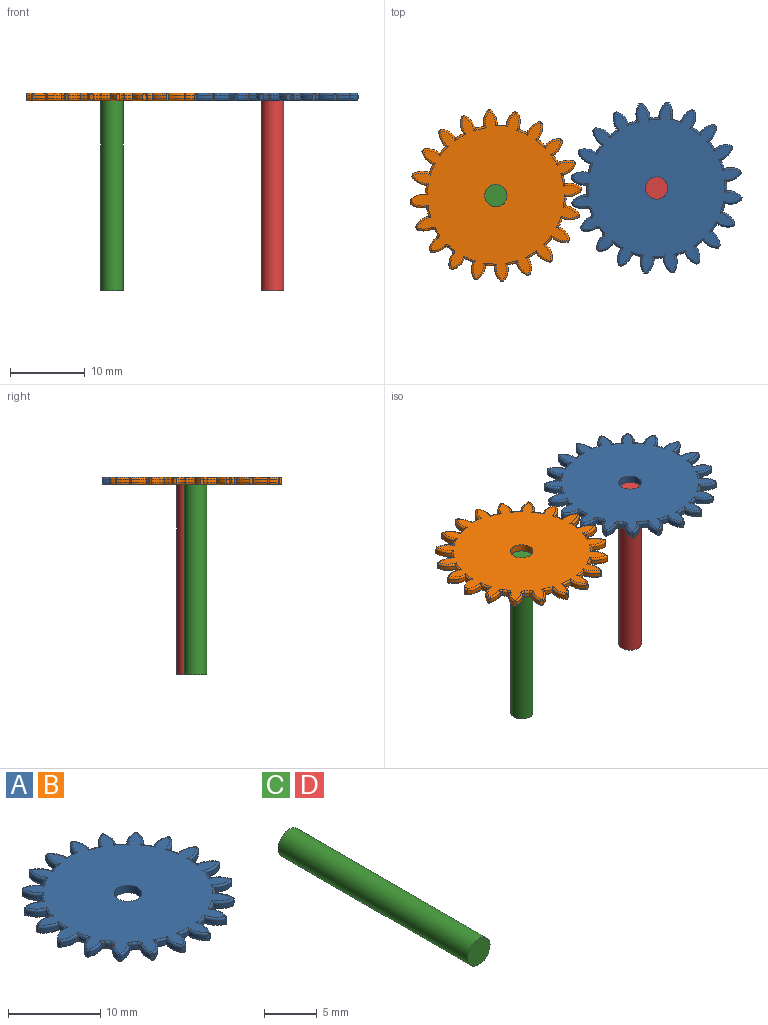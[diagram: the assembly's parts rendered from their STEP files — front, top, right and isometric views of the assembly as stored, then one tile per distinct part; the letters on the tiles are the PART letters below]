
ASSEMBLY  parts=4 mates=2
PART A: 214 faces, bbox 23.5x23.5x1 mm
  f0: cylinder r=2.61mm len=2.18mm, axis (0,0,-1), area 1.2mm2, adj f1,f79,f96,f200
  f1: cylinder r=9.41mm len=1.14mm, axis (0,0,-1), area 0.6mm2, adj f0,f2,f95,f201
  f2: cylinder r=2.61mm len=1.71mm, axis (0,0,-1), area 1.2mm2, adj f1,f3,f94,f203
  f3: plane 0.97x0.41mm, normal (-0.38,0.92,0), area 0.4mm2, adj f2,f4,f93,f94,f203,f205
  f4: cylinder r=2.61mm len=2.23mm, axis (0,0,-1), area 1.2mm2, adj f3,f5,f93,f205
  f5: cylinder r=9.41mm len=1mm, axis (0,0,-1), area 0.6mm2, adj f4,f6,f92,f207
  f6: cylinder r=2.61mm len=1.89mm, axis (0,0,-1), area 1.2mm2, adj f5,f7,f91,f209
  f7: plane 0.97x0.34mm, normal (-0.65,0.76,0), area 0.4mm2, adj f6,f8,f90,f91,f209,f211
  f8: cylinder r=2.61mm len=2.06mm, axis (0,0,-1), area 1.2mm2, adj f7,f9,f90,f211
  f9: cylinder r=9.41mm len=0.89mm, axis (0,0,-1), area 0.6mm2, adj f8,f10,f89,f213
  f10: cylinder r=2.61mm len=2.17mm, axis (0,0,-1), area 1.2mm2, adj f9,f11,f88,f212
  f11: plane 0.97x0.38mm, normal (-0.85,0.52,0), area 0.4mm2, adj f10,f12,f87,f88,f210,f212
  f12: cylinder r=2.61mm len=1.68mm, axis (0,0,-1), area 1.2mm2, adj f11,f13,f87,f210
  f13: cylinder r=9.41mm len=1.08mm, axis (0,0,-1), area 0.6mm2, adj f12,f14,f86,f208
  f14: cylinder r=2.61mm len=2.23mm, axis (0,0,-1), area 1.2mm2, adj f13,f15,f85,f206
  f15: plane 0.97x0.43mm, normal (-0.97,0.23,0), area 0.4mm2, adj f14,f16,f84,f85,f204,f206
  f16: cylinder r=2.61mm len=1.92mm, axis (0,0,-1), area 1.2mm2, adj f15,f17,f84,f204
  f17: cylinder r=9.41mm len=1.17mm, axis (0,0,-1), area 0.6mm2, adj f16,f18,f83,f202
  f18: cylinder r=2.61mm len=2.32mm, axis (0,0,-1), area 2.3mm2, adj f17,f19,f81,f82,f83,f169,f202
  f19: plane 0.75x0.44mm, normal (-1,-0.08,0), area 0.3mm2, adj f18,f20,f82,f169,f192
  f20: cylinder r=2.61mm len=2.18mm, axis (0,0,-1), area 1.2mm2, adj f19,f21,f173,f192
  f21: cylinder r=9.41mm len=1.14mm, axis (0,0,-1), area 0.6mm2, adj f20,f22,f176,f195
  f22: cylinder r=2.61mm len=1.71mm, axis (0,0,-1), area 1.2mm2, adj f21,f23,f180,f197
  f23: plane 0.73x0.41mm, normal (-0.92,-0.38,0), area 0.3mm2, adj f22,f24,f183,f197,f198
  f24: cylinder r=2.61mm len=2.02mm, axis (0,0,-1), area 1mm2, adj f23,f186,f193,f198
  f25: cylinder r=9.41mm len=0.59mm, axis (0,0,-1), area 0.3mm2, adj f187,f188,f193,f194
  f26: cylinder r=2.61mm len=1.76mm, axis (0,0,-1), area 1mm2, adj f27,f181,f188,f189
  f27: plane 0.97x0.34mm, normal (-0.76,-0.65,0), area 0.4mm2, adj f26,f28,f177,f181,f185,f189
  f28: cylinder r=2.61mm len=1.89mm, axis (0,0,-1), area 1mm2, adj f27,f177,f178,f185
  f29: cylinder r=9.41mm len=0.52mm, axis (0,0,-1), area 0.3mm2, adj f170,f171,f178,f179
  f30: cylinder r=2.61mm len=1.98mm, axis (0,0,-1), area 1mm2, adj f31,f165,f171,f172
  f31: plane 0.97x0.38mm, normal (-0.52,-0.85,0), area 0.4mm2, adj f30,f32,f163,f165,f168,f172
  f32: cylinder r=2.61mm len=1.68mm, axis (0,0,-1), area 1.2mm2, adj f31,f33,f163,f168
  f33: cylinder r=9.41mm len=1.08mm, axis (0,0,-1), area 0.6mm2, adj f32,f34,f161,f166
  f34: cylinder r=2.61mm len=2.23mm, axis (0,0,-1), area 1.2mm2, adj f33,f35,f159,f164
  f35: plane 0.97x0.43mm, normal (-0.23,-0.97,0), area 0.4mm2, adj f34,f36,f157,f159,f162,f164
  f36: cylinder r=2.61mm len=1.92mm, axis (0,0,-1), area 1.2mm2, adj f35,f37,f157,f162
  f37: cylinder r=9.41mm len=1.17mm, axis (0,0,-1), area 0.6mm2, adj f36,f38,f155,f160
  f38: cylinder r=2.61mm len=2.07mm, axis (0,0,-1), area 1.2mm2, adj f37,f39,f153,f158
  f39: plane 0.97x0.44mm, normal (0.08,-1,0), area 0.4mm2, adj f38,f40,f151,f153,f156,f158
  f40: cylinder r=2.61mm len=2.18mm, axis (0,0,-1), area 1.2mm2, adj f39,f41,f151,f156
  f41: cylinder r=9.41mm len=1.14mm, axis (0,0,-1), area 0.6mm2, adj f40,f42,f149,f154
  f42: cylinder r=2.61mm len=1.71mm, axis (0,0,-1), area 1.2mm2, adj f41,f43,f147,f152
  f43: plane 0.97x0.41mm, normal (0.38,-0.92,0), area 0.4mm2, adj f42,f44,f145,f147,f150,f152
  f44: cylinder r=2.61mm len=2.23mm, axis (0,0,-1), area 1.2mm2, adj f43,f45,f145,f150
  f45: cylinder r=9.41mm len=1mm, axis (0,0,-1), area 0.6mm2, adj f44,f46,f143,f148
  f46: cylinder r=2.61mm len=1.89mm, axis (0,0,-1), area 1.2mm2, adj f45,f47,f141,f146
  f47: plane 0.97x0.34mm, normal (0.65,-0.76,0), area 0.4mm2, adj f46,f48,f139,f141,f144,f146
  f48: cylinder r=2.61mm len=2.06mm, axis (0,0,-1), area 1.2mm2, adj f47,f49,f139,f144
  f49: cylinder r=9.41mm len=0.89mm, axis (0,0,-1), area 0.6mm2, adj f48,f50,f137,f142
  f50: cylinder r=2.61mm len=2.17mm, axis (0,0,-1), area 1.2mm2, adj f49,f51,f135,f140
  f51: plane 0.97x0.38mm, normal (0.85,-0.52,0), area 0.4mm2, adj f50,f52,f133,f135,f138,f140
  f52: cylinder r=2.61mm len=1.68mm, axis (0,0,-1), area 1.2mm2, adj f51,f53,f133,f138
  f53: cylinder r=9.41mm len=1.08mm, axis (0,0,-1), area 0.6mm2, adj f52,f54,f131,f136
  f54: cylinder r=2.61mm len=2.23mm, axis (0,0,-1), area 1.2mm2, adj f53,f55,f129,f134
  f55: plane 0.97x0.43mm, normal (0.97,-0.23,0), area 0.4mm2, adj f54,f56,f127,f129,f132,f134
  f56: cylinder r=2.61mm len=1.92mm, axis (0,0,-1), area 1.2mm2, adj f55,f57,f127,f132
  f57: cylinder r=9.41mm len=1.17mm, axis (0,0,-1), area 0.6mm2, adj f56,f58,f125,f130
  f58: cylinder r=2.61mm len=2.07mm, axis (0,0,-1), area 1.2mm2, adj f57,f59,f123,f128
  f59: plane 0.97x0.44mm, normal (1,0.08,0), area 0.4mm2, adj f58,f60,f121,f123,f126,f128
  f60: cylinder r=2.61mm len=2.18mm, axis (0,0,-1), area 1.2mm2, adj f59,f61,f121,f126
  f61: cylinder r=9.41mm len=1.14mm, axis (0,0,-1), area 0.6mm2, adj f60,f62,f119,f124
  f62: cylinder r=2.61mm len=1.71mm, axis (0,0,-1), area 1.2mm2, adj f61,f63,f117,f122
  f63: plane 0.97x0.41mm, normal (0.92,0.38,0), area 0.4mm2, adj f62,f64,f115,f117,f120,f122
  f64: cylinder r=2.61mm len=2.23mm, axis (0,0,-1), area 1.2mm2, adj f63,f65,f115,f120
  f65: cylinder r=9.41mm len=1mm, axis (0,0,-1), area 0.6mm2, adj f64,f66,f113,f118
  f66: cylinder r=2.61mm len=1.89mm, axis (0,0,-1), area 1.2mm2, adj f65,f67,f111,f116
  f67: plane 0.97x0.34mm, normal (0.76,0.65,0), area 0.4mm2, adj f66,f68,f109,f111,f114,f116
  f68: cylinder r=2.61mm len=2.06mm, axis (0,0,-1), area 1.2mm2, adj f67,f69,f109,f114
  f69: cylinder r=9.41mm len=0.89mm, axis (0,0,-1), area 0.6mm2, adj f68,f70,f107,f112
  f70: cylinder r=2.61mm len=2.17mm, axis (0,0,-1), area 1.2mm2, adj f69,f71,f105,f110
  f71: plane 0.97x0.38mm, normal (0.52,0.85,0), area 0.4mm2, adj f70,f72,f103,f105,f108,f110
  f72: cylinder r=2.61mm len=1.68mm, axis (0,0,-1), area 1.2mm2, adj f71,f73,f103,f108
  f73: cylinder r=9.41mm len=1.08mm, axis (0,0,-1), area 0.6mm2, adj f72,f74,f101,f106
  f74: cylinder r=2.61mm len=2.23mm, axis (0,0,-1), area 1.2mm2, adj f73,f75,f99,f104
  f75: plane 0.97x0.43mm, normal (0.23,0.97,0), area 0.4mm2, adj f74,f76,f97,f99,f102,f104
  f76: cylinder r=2.61mm len=1.92mm, axis (0,0,-1), area 1.2mm2, adj f75,f77,f97,f102
  f77: cylinder r=9.41mm len=1.67mm, axis (0,0,-1), area 0.9mm2, adj f76,f78,f81,f97,f100,f199
  f78: cylinder r=2.61mm len=2.07mm, axis (0,0,-1), area 1.2mm2, adj f77,f79,f98,f199
  f79: plane 0.97x0.44mm, normal (-0.08,1,0), area 0.4mm2, adj f0,f78,f96,f98,f199,f200
  f80: cylinder r=1.5mm len=3mm, axis (0,0,-1), area 9.4mm2, adj f81,f82
  f81: plane 22.67x22.58mm, normal (0,0,1), area 302.4mm2, adj f18,f77,f80,f97,f99,f101,f103,f105
  f82: plane 22.81x22.67mm, normal (0,0,-1), area 302.1mm2, adj f18,f19,f80,f83,f84,f85,f86,f87
  f83: torus R=9.16mm, axis (0,0,1), area 0.5mm2, adj f17,f18,f82,f84
  f84: torus R=2.36mm, axis (0,0,1), area 0.9mm2, adj f15,f16,f82,f83,f85
  f85: torus R=2.36mm, axis (0,0,1), area 0.9mm2, adj f14,f15,f82,f84,f86
  f86: torus R=9.16mm, axis (0,0,1), area 0.5mm2, adj f13,f82,f85,f87
  f87: torus R=2.36mm, axis (0,0,1), area 0.9mm2, adj f11,f12,f82,f86,f88
  f88: torus R=2.36mm, axis (0,0,1), area 0.9mm2, adj f10,f11,f82,f87,f89
  f89: torus R=9.16mm, axis (0,0,1), area 0.5mm2, adj f9,f82,f88,f90
  f90: torus R=2.36mm, axis (0,0,1), area 0.9mm2, adj f7,f8,f82,f89,f91
  f91: torus R=2.36mm, axis (0,0,1), area 0.9mm2, adj f6,f7,f82,f90,f92
  f92: torus R=9.16mm, axis (0,0,1), area 0.5mm2, adj f5,f82,f91,f93
  f93: torus R=2.36mm, axis (0,0,1), area 0.9mm2, adj f3,f4,f82,f92,f94
  f94: torus R=2.36mm, axis (0,0,1), area 0.9mm2, adj f2,f3,f82,f93,f95
  f95: torus R=9.16mm, axis (0,0,1), area 0.5mm2, adj f1,f82,f94,f96
  f96: torus R=2.36mm, axis (0,0,1), area 0.9mm2, adj f0,f79,f82,f95,f98
  f97: torus R=2.36mm, axis (0,0,1), area 0.9mm2, adj f75,f76,f77,f81,f99
  f98: torus R=2.36mm, axis (0,0,1), area 0.9mm2, adj f78,f79,f82,f96,f100
  f99: torus R=2.36mm, axis (0,0,1), area 0.9mm2, adj f74,f75,f81,f97,f101
  f100: torus R=9.16mm, axis (0,0,1), area 0.5mm2, adj f77,f82,f98,f102
  f101: torus R=9.16mm, axis (0,0,1), area 0.5mm2, adj f73,f81,f99,f103
  f102: torus R=2.36mm, axis (0,0,1), area 0.9mm2, adj f75,f76,f82,f100,f104
  f103: torus R=2.36mm, axis (0,0,1), area 0.9mm2, adj f71,f72,f81,f101,f105
  f104: torus R=2.36mm, axis (0,0,1), area 0.9mm2, adj f74,f75,f82,f102,f106
  f105: torus R=2.36mm, axis (0,0,1), area 0.9mm2, adj f70,f71,f81,f103,f107
  f106: torus R=9.16mm, axis (0,0,1), area 0.5mm2, adj f73,f82,f104,f108
  f107: torus R=9.16mm, axis (0,0,1), area 0.5mm2, adj f69,f81,f105,f109
  f108: torus R=2.36mm, axis (0,0,1), area 0.9mm2, adj f71,f72,f82,f106,f110
  f109: torus R=2.36mm, axis (0,0,1), area 0.9mm2, adj f67,f68,f81,f107,f111
  f110: torus R=2.36mm, axis (0,0,1), area 0.9mm2, adj f70,f71,f82,f108,f112
  f111: torus R=2.36mm, axis (0,0,1), area 0.9mm2, adj f66,f67,f81,f109,f113
  f112: torus R=9.16mm, axis (0,0,1), area 0.5mm2, adj f69,f82,f110,f114
  f113: torus R=9.16mm, axis (0,0,1), area 0.5mm2, adj f65,f81,f111,f115
  f114: torus R=2.36mm, axis (0,0,1), area 0.9mm2, adj f67,f68,f82,f112,f116
  f115: torus R=2.36mm, axis (0,0,1), area 0.9mm2, adj f63,f64,f81,f113,f117
  f116: torus R=2.36mm, axis (0,0,1), area 0.9mm2, adj f66,f67,f82,f114,f118
  f117: torus R=2.36mm, axis (0,0,1), area 0.9mm2, adj f62,f63,f81,f115,f119
  f118: torus R=9.16mm, axis (0,0,1), area 0.5mm2, adj f65,f82,f116,f120
  f119: torus R=9.16mm, axis (0,0,1), area 0.5mm2, adj f61,f81,f117,f121
  f120: torus R=2.36mm, axis (0,0,1), area 0.9mm2, adj f63,f64,f82,f118,f122
  f121: torus R=2.36mm, axis (0,0,1), area 0.9mm2, adj f59,f60,f81,f119,f123
  f122: torus R=2.36mm, axis (0,0,1), area 0.9mm2, adj f62,f63,f82,f120,f124
  f123: torus R=2.36mm, axis (0,0,1), area 0.9mm2, adj f58,f59,f81,f121,f125
  f124: torus R=9.16mm, axis (0,0,1), area 0.5mm2, adj f61,f82,f122,f126
  f125: torus R=9.16mm, axis (0,0,1), area 0.5mm2, adj f57,f81,f123,f127
  f126: torus R=2.36mm, axis (0,0,1), area 0.9mm2, adj f59,f60,f82,f124,f128
  f127: torus R=2.36mm, axis (0,0,1), area 0.9mm2, adj f55,f56,f81,f125,f129
  f128: torus R=2.36mm, axis (0,0,1), area 0.9mm2, adj f58,f59,f82,f126,f130
  f129: torus R=2.36mm, axis (0,0,1), area 0.9mm2, adj f54,f55,f81,f127,f131
  f130: torus R=9.16mm, axis (0,0,1), area 0.5mm2, adj f57,f82,f128,f132
  f131: torus R=9.16mm, axis (0,0,1), area 0.5mm2, adj f53,f81,f129,f133
  f132: torus R=2.36mm, axis (0,0,1), area 0.9mm2, adj f55,f56,f82,f130,f134
  f133: torus R=2.36mm, axis (0,0,1), area 0.9mm2, adj f51,f52,f81,f131,f135
  f134: torus R=2.36mm, axis (0,0,1), area 0.9mm2, adj f54,f55,f82,f132,f136
  f135: torus R=2.36mm, axis (0,0,1), area 0.9mm2, adj f50,f51,f81,f133,f137
  f136: torus R=9.16mm, axis (0,0,1), area 0.5mm2, adj f53,f82,f134,f138
  f137: torus R=9.16mm, axis (0,0,1), area 0.5mm2, adj f49,f81,f135,f139
  f138: torus R=2.36mm, axis (0,0,1), area 0.9mm2, adj f51,f52,f82,f136,f140
  f139: torus R=2.36mm, axis (0,0,1), area 0.9mm2, adj f47,f48,f81,f137,f141
  f140: torus R=2.36mm, axis (0,0,1), area 0.9mm2, adj f50,f51,f82,f138,f142
  f141: torus R=2.36mm, axis (0,0,1), area 0.9mm2, adj f46,f47,f81,f139,f143
  f142: torus R=9.16mm, axis (0,0,1), area 0.5mm2, adj f49,f82,f140,f144
  f143: torus R=9.16mm, axis (0,0,1), area 0.5mm2, adj f45,f81,f141,f145
  f144: torus R=2.36mm, axis (0,0,1), area 0.9mm2, adj f47,f48,f82,f142,f146
  f145: torus R=2.36mm, axis (0,0,1), area 0.9mm2, adj f43,f44,f81,f143,f147
  f146: torus R=2.36mm, axis (0,0,1), area 0.9mm2, adj f46,f47,f82,f144,f148
  f147: torus R=2.36mm, axis (0,0,1), area 0.9mm2, adj f42,f43,f81,f145,f149
  f148: torus R=9.16mm, axis (0,0,1), area 0.5mm2, adj f45,f82,f146,f150
  f149: torus R=9.16mm, axis (0,0,1), area 0.5mm2, adj f41,f81,f147,f151
  f150: torus R=2.36mm, axis (0,0,1), area 0.9mm2, adj f43,f44,f82,f148,f152
  f151: torus R=2.36mm, axis (0,0,1), area 0.9mm2, adj f39,f40,f81,f149,f153
  f152: torus R=2.36mm, axis (0,0,1), area 0.9mm2, adj f42,f43,f82,f150,f154
  f153: torus R=2.36mm, axis (0,0,1), area 0.9mm2, adj f38,f39,f81,f151,f155
  f154: torus R=9.16mm, axis (0,0,1), area 0.5mm2, adj f41,f82,f152,f156
  f155: torus R=9.16mm, axis (0,0,1), area 0.5mm2, adj f37,f81,f153,f157
  f156: torus R=2.36mm, axis (0,0,1), area 0.9mm2, adj f39,f40,f82,f154,f158
  f157: torus R=2.36mm, axis (0,0,1), area 0.9mm2, adj f35,f36,f81,f155,f159
  f158: torus R=2.36mm, axis (0,0,1), area 0.9mm2, adj f38,f39,f82,f156,f160
  f159: torus R=2.36mm, axis (0,0,1), area 0.9mm2, adj f34,f35,f81,f157,f161
  f160: torus R=9.16mm, axis (0,0,1), area 0.5mm2, adj f37,f82,f158,f162
  f161: torus R=9.16mm, axis (0,0,1), area 0.5mm2, adj f33,f81,f159,f163
  f162: torus R=2.36mm, axis (0,0,1), area 0.9mm2, adj f35,f36,f82,f160,f164
  f163: torus R=2.36mm, axis (0,0,1), area 0.9mm2, adj f31,f32,f81,f161,f165
  f164: torus R=2.36mm, axis (0,0,1), area 0.9mm2, adj f34,f35,f82,f162,f166
  f165: torus R=2.36mm, axis (0,0,1), area 0.8mm2, adj f30,f31,f81,f163,f167
  f166: torus R=9.16mm, axis (0,0,1), area 0.5mm2, adj f33,f82,f164,f168
  f167: torus R=0.5mm, axis (0,0,1), area 0.2mm2, adj f81,f165,f170,f171
  f168: torus R=2.36mm, axis (0,0,1), area 0.9mm2, adj f31,f32,f82,f166,f172
  f169: cylinder r=0.25mm len=0.66mm, axis (-0.08,1,0), area 0.2mm2, adj f18,f19,f81,f173
  f170: torus R=9.16mm, axis (0,0,1), area 0.3mm2, adj f29,f81,f167,f174
  f171: cylinder r=0.25mm len=0.5mm, axis (0,0,1), area 0.2mm2, adj f29,f30,f167,f175
  f172: torus R=2.36mm, axis (0,0,1), area 0.8mm2, adj f30,f31,f82,f168,f175
  f173: torus R=2.36mm, axis (0,0,1), area 0.9mm2, adj f20,f81,f169,f176
  f174: torus R=0.5mm, axis (0,0,1), area 0.2mm2, adj f81,f170,f177,f178
  f175: torus R=0.5mm, axis (0,0,1), area 0.2mm2, adj f82,f171,f172,f179
  f176: torus R=9.16mm, axis (0,0,1), area 0.5mm2, adj f21,f81,f173,f180
  f177: torus R=2.36mm, axis (0,0,1), area 0.8mm2, adj f27,f28,f81,f174,f181
  f178: cylinder r=0.25mm len=0.5mm, axis (0,0,1), area 0.2mm2, adj f28,f29,f174,f182
  f179: torus R=9.16mm, axis (0,0,1), area 0.3mm2, adj f29,f82,f175,f182
  f180: torus R=2.36mm, axis (0,0,1), area 0.9mm2, adj f22,f81,f176,f183
  f181: torus R=2.36mm, axis (0,0,1), area 0.8mm2, adj f26,f27,f81,f177,f184
  f182: torus R=0.5mm, axis (0,0,1), area 0.2mm2, adj f82,f178,f179,f185
  f183: cylinder r=0.25mm len=0.5mm, axis (-0.38,0.92,0), area 0.1mm2, adj f23,f81,f180,f186
  f184: torus R=0.5mm, axis (0,0,1), area 0.2mm2, adj f81,f181,f187,f188
  f185: torus R=2.36mm, axis (0,0,1), area 0.8mm2, adj f27,f28,f82,f182,f189
  f186: torus R=2.36mm, axis (0,0,1), area 0.8mm2, adj f24,f81,f183,f190
  f187: torus R=9.16mm, axis (0,0,1), area 0.3mm2, adj f25,f81,f184,f190
  f188: cylinder r=0.25mm len=0.5mm, axis (0,0,1), area 0.2mm2, adj f25,f26,f184,f191
  f189: torus R=2.36mm, axis (0,0,1), area 0.8mm2, adj f26,f27,f82,f185,f191
  f190: torus R=0.5mm, axis (0,0,1), area 0.2mm2, adj f81,f186,f187,f193
  f191: torus R=0.5mm, axis (0,0,1), area 0.2mm2, adj f82,f188,f189,f194
  f192: torus R=2.36mm, axis (0,0,1), area 0.9mm2, adj f19,f20,f82,f195
  f193: cylinder r=0.25mm len=0.5mm, axis (0,0,1), area 0.2mm2, adj f24,f25,f190,f196
  f194: torus R=9.16mm, axis (0,0,1), area 0.3mm2, adj f25,f82,f191,f196
  f195: torus R=9.16mm, axis (0,0,1), area 0.5mm2, adj f21,f82,f192,f197
  f196: torus R=0.5mm, axis (0,0,1), area 0.2mm2, adj f82,f193,f194,f198
  f197: torus R=2.36mm, axis (0,0,1), area 0.9mm2, adj f22,f23,f82,f195,f198
  f198: torus R=2.36mm, axis (0,0,1), area 0.8mm2, adj f23,f24,f82,f196,f197
  f199: torus R=2.36mm, axis (0,0,1), area 0.9mm2, adj f77,f78,f79,f81,f200
  f200: torus R=2.36mm, axis (0,0,1), area 0.9mm2, adj f0,f79,f81,f199,f201
  f201: torus R=9.16mm, axis (0,0,1), area 0.5mm2, adj f1,f81,f200,f203
  f202: torus R=9.16mm, axis (0,0,1), area 0.5mm2, adj f17,f18,f81,f204
  f203: torus R=2.36mm, axis (0,0,1), area 0.9mm2, adj f2,f3,f81,f201,f205
  f204: torus R=2.36mm, axis (0,0,1), area 0.9mm2, adj f15,f16,f81,f202,f206
  f205: torus R=2.36mm, axis (0,0,1), area 0.9mm2, adj f3,f4,f81,f203,f207
  f206: torus R=2.36mm, axis (0,0,1), area 0.9mm2, adj f14,f15,f81,f204,f208
  f207: torus R=9.16mm, axis (0,0,1), area 0.5mm2, adj f5,f81,f205,f209
  f208: torus R=9.16mm, axis (0,0,1), area 0.5mm2, adj f13,f81,f206,f210
  f209: torus R=2.36mm, axis (0,0,1), area 0.9mm2, adj f6,f7,f81,f207,f211
  f210: torus R=2.36mm, axis (0,0,1), area 0.9mm2, adj f11,f12,f81,f208,f212
  f211: torus R=2.36mm, axis (0,0,1), area 0.9mm2, adj f7,f8,f81,f209,f213
  f212: torus R=2.36mm, axis (0,0,1), area 0.9mm2, adj f10,f11,f81,f210,f213
  f213: torus R=9.16mm, axis (0,0,1), area 0.5mm2, adj f9,f81,f211,f212
PART B: same geometry as A
PART C: 3 faces, bbox 3x25.4x3 mm
  f0: cylinder r=1.5mm len=25.4mm, axis (0,1,0), area 239.2mm2, adj f1,f2
  f1: plane 3x3mm, normal (0,-1,0), area 7.1mm2, adj f0
  f2: plane 3x3mm, normal (0,1,0), area 7.1mm2, adj f0
PART D: same geometry as C
PLACE A rot(axis=(0,0,-1),11.8deg) t=(21.35,1.03,0)mm
PLACE B rot(axis=(0,0,-1),0.2deg) t=(-0.15,0.01,0)mm
PLACE C rot(axis=(1,0,0),90deg) t=(-0.15,0.01,0)mm
PLACE D rot(axis=(-0.99,0.1,-0.1),90.6deg) t=(21.35,1.03,-25.4)mm
MATE revolute D.f0 <-> A.f1  axis (0,0,1) through (21.35,1.03,0)mm
MATE revolute C.f0 <-> B.f1  axis (0,0,1) through (-0.15,0.01,0)mm
